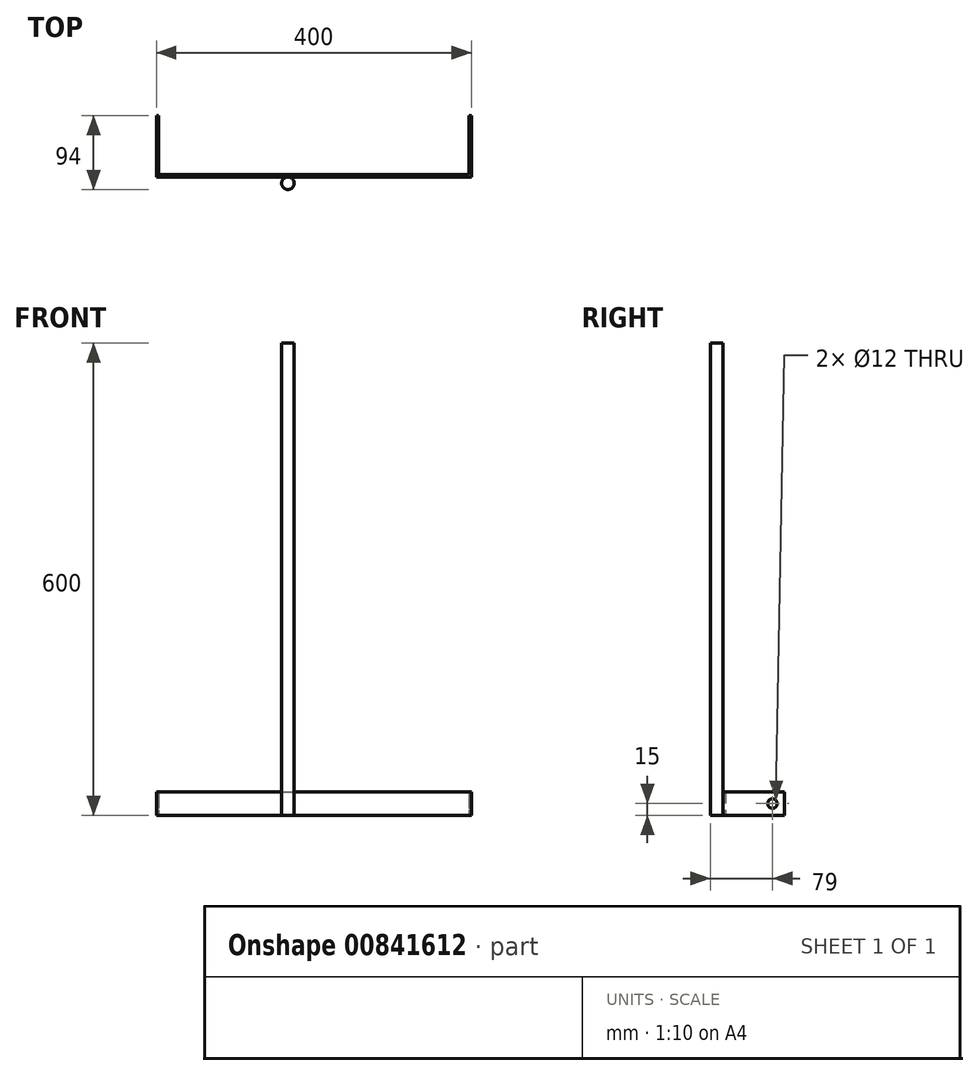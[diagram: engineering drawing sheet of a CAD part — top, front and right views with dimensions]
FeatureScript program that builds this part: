
annotation { "Feature Type Name" : "Feature", "Feature Type Description" : "" }
export const myFeature = defineFeature(function(context is Context, id is Id, definition is map)
    precondition{}
    {
        {
            var Q0;
            Q0=qCreatedBy(makeId("Top.planeOp"),FACE);
            var sketch = newSketch(context, id + "F0", { "sketchPlane" : qUnion([Q0])});
            skLineSegment(sketch, "E0.bottom", {"start": v(-167.03, 0) * mm, "end": v(232.97, 0) * mm});
            skLineSegment(sketch, "E0.top", {"start": v(-167.03, 3) * mm, "end": v(232.97, 3) * mm});
            skLineSegment(sketch, "E0.left", {"start": v(-167.03, 0) * mm, "end": v(-167.03, 3) * mm});
            skLineSegment(sketch, "E0.right", {"start": v(232.97, 0) * mm, "end": v(232.97, 3) * mm});
            skLineSegment(sketch, "E1.bottom", {"start": v(-167.03, 3) * mm, "end": v(-164.03, 3) * mm});
            skLineSegment(sketch, "E1.top", {"start": v(-167.03, 78) * mm, "end": v(-164.03, 78) * mm});
            skLineSegment(sketch, "E1.left", {"start": v(-167.03, 3) * mm, "end": v(-167.03, 78) * mm});
            skLineSegment(sketch, "E1.right", {"start": v(-164.03, 3) * mm, "end": v(-164.03, 78) * mm});
            skLineSegment(sketch, "E2.bottom", {"start": v(232.97, 3) * mm, "end": v(229.97, 3) * mm});
            skLineSegment(sketch, "E2.top", {"start": v(232.97, 78) * mm, "end": v(229.97, 78) * mm});
            skLineSegment(sketch, "E2.left", {"start": v(232.97, 3) * mm, "end": v(232.97, 78) * mm});
            skLineSegment(sketch, "E2.right", {"start": v(229.97, 3) * mm, "end": v(229.97, 78) * mm});
            skSolve(sketch);
        }
        {
            var Q0;
            Q0 = qSketchRegion(id + "F0", true);
            extrude(context, id + "F1", {"entities" : qUnion([Q0]), "depth" : 30 * mm, "offsetDistance" : 25 * mm});
        }
        {
            var Q0;
            Q0=makeQuery(id+"F1.opExtrude","SWEPT_FACE",FACE,{"disambiguationData":[OSD([sQuery(id+"F0.wireOp",EDGE,"E0.left"),sQuery(id+"F0.wireOp",EDGE,"E1.left")])]});
            var sketch = newSketch(context, id + "F2", { "sketchPlane" : qUnion([Q0])});
            skCircle(sketch, "E3", {"center": v(-63, 15) * mm, "radius": 6 * mm});
            skSolve(sketch);
        }
        {
            var Q0;
            Q0 = qSketchRegion(id + "F2", true);
            extrude(context, id + "F3", {"entities" : qUnion([Q0]), "operationType" : NewBodyOperationType.REMOVE, "oppositeDirection" : true, "depth" : 500 * mm, "offsetDistance" : 25 * mm});
        }
        {
            var Q0;
            Q0=qCreatedBy(makeId("Top.planeOp"),FACE);
            var sketch = newSketch(context, id + "F4", { "sketchPlane" : qUnion([Q0])});
            skCircle(sketch, "E4", {"center": v(0, -8) * mm, "radius": 8 * mm});
            skSolve(sketch);
        }
        {
            var Q0;
            Q0=makeQuery(id+"F4.imprint","IMPRINT",FACE,{"disambiguationData":[TD([[makeQuery(id+"F4.imprint","IMPRINT",EDGE,{"derivedFrom":sQuery(id+"F4.wireOp",EDGE,"E4")}),1.0]])]});
            extrude(context, id + "F5", {"entities" : qUnion([Q0]), "operationType" : NewBodyOperationType.ADD, "depth" : 600 * mm, "offsetDistance" : 25 * mm});
        }
    });
